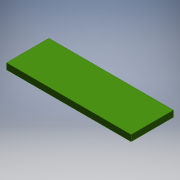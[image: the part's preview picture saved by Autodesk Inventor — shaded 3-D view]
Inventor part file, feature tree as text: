
AUTODESK INVENTOR PART (.ipt)
format: ipt  version: 2016 (Build 200138000, 138)  size: 95,744 bytes
history: native  units: mm
features: extrude x1, sketch x1
ambient origin geometry x8: Origin, YZ Plane, XZ Plane, XY Plane, X Axis, Y Axis, Z Axis, Center Point
bodies: Solid1 (feature_tree)
feature tree (2):
  extrude  "Extrusion1"  Depth=40.0mm
  sketch  "Sketch1"  dims[d0=13.6mm d1=40.0mm d2=20.0mm d3=6.8mm d4=2.0mm d5=0.0mm]
